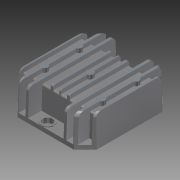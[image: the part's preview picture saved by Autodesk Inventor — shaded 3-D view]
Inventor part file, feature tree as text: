
AUTODESK INVENTOR PART (.ipt)
format: ipt  version: 2014 SP1 (Build 180222100, 222)  size: 353,792 bytes
history: native  units: in
note: dims shown in document units (in); Inventor stores cm internally (conversion verified against a paired STEP export)
features: extrude x8, sketch x7, plane x3, fillet x3, mirror x2, projected_geometry x1
ambient origin geometry x8: Origin, YZ Plane, XZ Plane, XY Plane, X Axis, Y Axis, Z Axis, Center Point
bodies: Solid1 (feature_tree)
feature tree (24):
  sketch  "Sketch1"  dims[d0=0.906in d1=-0.0137in d4=0.25in d5=0.25in]
  extrude  "Extrusion1"  Depth=0.906in
  extrude  "Extrusion3"  Depth=0.047in
  plane  "Work Plane1"
  mirror  "Mirror1"
  plane  "Work Plane2"
  extrude  "Extrusion4"  Depth=0.079in
  extrude  "Extrusion5"  Depth=0.079in
  extrude  "Extrusion6"  Depth=0.2403in
  extrude  "Extrusion7"  TaperAngle=0.0deg  [1 undecoded]
  fillet  "Fillet1"  Radius=0.787in
  fillet  "Fillet2"  Radius=0.787in
  fillet  "Fillet3"  Radius=0.787in
  extrude  "Extrusion8"  Depth=0.125in
  plane  "Work Plane3"
  mirror  "Mirror2"
  extrude  "Extrusion9"  Depth=0.05in
  sketch  "Sketch4"  dims[d6=0.25in d7=0.047in]
  sketch  "Sketch5"  dims[d8=0.202in d9=0.079in]
  sketch  "Sketch7"  dims[d10=0.202in d11=0.079in]
  sketch  "Sketch8"  dims[d12=0.787in d13=0.0in d14=0.2403in]
  sketch  "Sketch9"  dims[d16=0.182in d17=0.0in d18=0.787in d19=0.0in d20=0.787in d21=0.0in d22=0.787in d23=0.0in]
  projected_geometry  "Projected Loop1"
  sketch  "Sketch10"  dims[d24=0.787in d25=0.0in d26=0.125in d27=0.05in d28=0.05in d29=0.2in d32=1.0in d33=0.787in d34=0.0in d35=0.375in d37=0.02in d38=-0.0137in]
note: 1 required parameter value undecoded (feature->parameter linkage not recoverable at this tier; creation-order binding heuristic only, values carry confidence <= 0.55)
